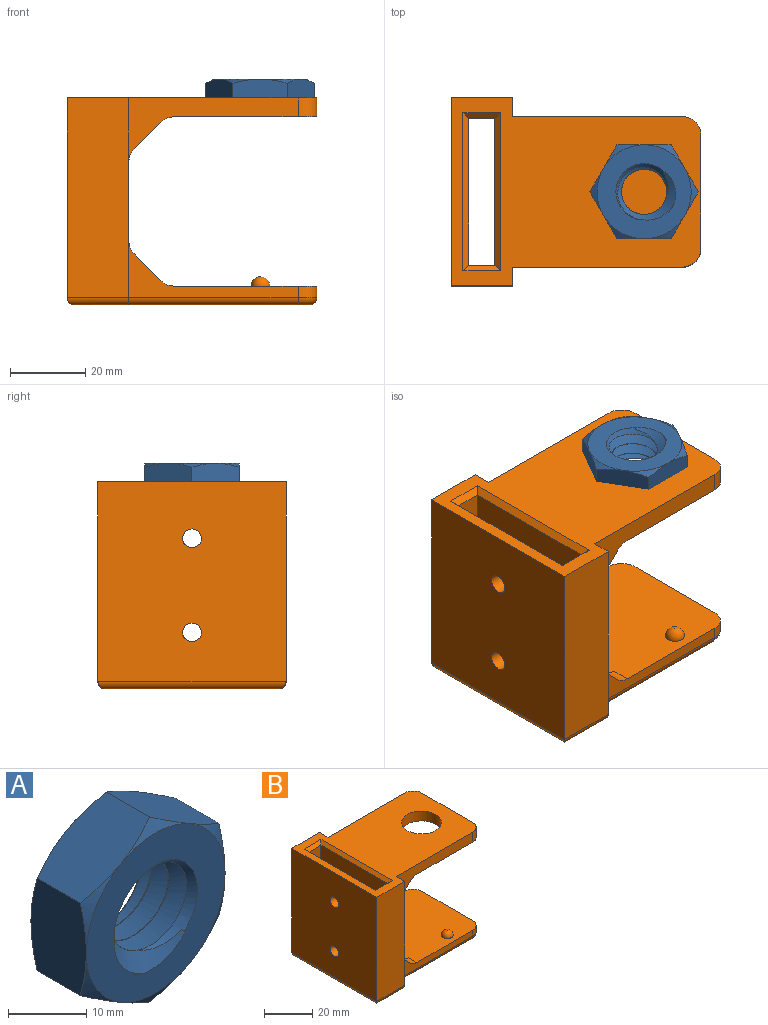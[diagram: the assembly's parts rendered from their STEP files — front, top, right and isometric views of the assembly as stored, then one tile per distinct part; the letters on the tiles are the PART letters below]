
ASSEMBLY  parts=2 mates=1
PART A: 26 faces, bbox 30.1x15x30.1 mm
  f0: cylinder r=6mm len=12mm, axis (0,1,0), area 8.6mm2, adj f21,f22,f23,f24
  f1: plane 25.37x25.37mm, normal (0,-1,0), area 303.3mm2, adj f5,f6,f8,f10,f12,f14,f22,f23
  f2: plane 25.48x25.48mm, normal (0,1,0), area 303mm2, adj f3,f4,f7,f9,f11,f13,f21,f23
  f3: cone r=20.25mm half-angle=60deg, axis (0,-1,0), area 15.4mm2, adj f2,f15,f16
  f4: cone r=20.25mm half-angle=60deg, axis (0,-1,0), area 15.4mm2, adj f2,f15,f20
  f5: cone r=20.25mm half-angle=60deg, axis (0,1,0), area 15.4mm2, adj f1,f15,f16
  f6: cone r=20.25mm half-angle=60deg, axis (0,1,0), area 15.4mm2, adj f1,f15,f20
  f7: cone r=20.25mm half-angle=60deg, axis (0,-1,0), area 15.4mm2, adj f2,f16,f17
  f8: cone r=20.25mm half-angle=60deg, axis (0,1,0), area 15.4mm2, adj f1,f16,f17
  f9: cone r=20.25mm half-angle=60deg, axis (0,-1,0), area 15.4mm2, adj f2,f17,f18
  f10: cone r=20.25mm half-angle=60deg, axis (0,1,0), area 15.4mm2, adj f1,f17,f18
  f11: cone r=20.25mm half-angle=60deg, axis (0,-1,0), area 15.4mm2, adj f2,f18,f19
  f12: cone r=20.25mm half-angle=60deg, axis (0,1,0), area 15.4mm2, adj f1,f18,f19
  f13: cone r=20.25mm half-angle=60deg, axis (0,-1,0), area 15.4mm2, adj f2,f19,f20
  f14: cone r=20.25mm half-angle=60deg, axis (0,1,0), area 15.4mm2, adj f1,f19,f20
  f15: plane 15.63x11.2mm, normal (1,0,0), area 133.3mm2, adj f3,f4,f5,f6,f16,f20
  f16: plane 13.69x11.19mm, normal (0.5,0,-0.87), area 133.3mm2, adj f3,f5,f7,f8,f15,f17
  f17: plane 13.69x11.19mm, normal (-0.5,0,-0.87), area 133.3mm2, adj f7,f8,f9,f10,f16,f18
  f18: plane 15.63x11.2mm, normal (-1,0,0), area 133.3mm2, adj f9,f10,f11,f12,f17,f19
  f19: plane 13.69x11.19mm, normal (-0.5,0,0.87), area 133.3mm2, adj f11,f12,f13,f14,f18,f20
  f20: plane 13.69x11.19mm, normal (0.5,0,0.87), area 133.3mm2, adj f4,f6,f13,f14,f15,f19
  f21: cone r=7.5mm half-angle=45deg, axis (0,1,0), area 28.9mm2, adj f0,f2,f23,f24
  f22: cone r=6mm half-angle=45deg, axis (0,-1,0), area 29.4mm2, adj f0,f1,f23,f24,f25
  f23: bspline ~19.86x17.2mm, area 410.3mm2, adj f0,f1,f2,f21,f22,f24
  f24: bspline ~19.86x17.2mm, area 410.2mm2, adj f0,f1,f2,f21,f22,f23,f25
  f25: plane 0.42x0.39mm, normal (-0.72,0,-0.69), area 0mm2, adj f1,f22,f24
PART B: 61 faces, bbox 66.8x50x55 mm
  f0: plane 7.07x7.07mm, normal (0.71,0,-0.71), area 50mm2, adj f11,f29,f39,f45
  f1: cylinder r=2.5mm len=5mm, axis (-1,0,0), area 74.6mm2, adj f8,f21
  f2: plane 7.07x7.07mm, normal (0.71,0,0.71), area 50mm2, adj f12,f28,f40,f46
  f3: cylinder r=2.5mm len=5mm, axis (-1,0,0), area 74.6mm2, adj f8,f21
  f4: plane 62.4x46mm, normal (0,0,-1), area 1965.5mm2, adj f14,f18,f31,f32,f33,f34,f53,f54
  f5: plane 66.4x50mm, normal (0,0,1), area 2174.4mm2, adj f10,f11,f12,f13,f14,f15,f16,f17
  f6: plane 30x3mm, normal (1,0,0), area 90mm2, adj f7,f48,f50,f55
  f7: plane 50x40mm, normal (0,0,1), area 1829.3mm2, adj f6,f8,f11,f12,f27,f28,f40,f43
  f8: plane 45x40mm, normal (1,0,0), area 1519.3mm2, adj f1,f3,f7,f9,f11,f12,f27,f28
  f9: plane 50x40mm, normal (0,0,-1), area 1654.7mm2, adj f8,f10,f11,f12,f13,f29,f30,f39
  f10: plane 30x5mm, normal (1,0,0), area 150mm2, adj f5,f9,f47,f49
  f11: plane 53x45.1mm, normal (0,1,0), area 467.5mm2, adj f0,f5,f7,f8,f9,f18,f24,f39
  f12: plane 53x45.1mm, normal (0,-1,0), area 467.5mm2, adj f2,f5,f7,f8,f9,f14,f23,f40
  f13: cylinder r=8.25mm len=16.5mm, axis (0,0,1), area 259.2mm2, adj f5,f9
  f14: plane 55x7mm, normal (1,0,0), area 275mm2, adj f4,f5,f12,f15,f57,f60
  f15: plane 53x16.3mm, normal (0,-1,0), area 863.9mm2, adj f5,f14,f17,f60
  f16: plane 53x16.3mm, normal (0,1,0), area 863.9mm2, adj f5,f17,f18,f58
  f17: plane 53x50mm, normal (-1,0,0), area 2610.7mm2, adj f5,f15,f16,f25,f26,f59
  f18: plane 55x7mm, normal (1,0,0), area 275mm2, adj f4,f5,f11,f16,f53,f58
  f19: plane 52x39mm, normal (1,0,0), area 1988.7mm2, adj f20,f22,f25,f26,f32,f36
  f20: plane 52x7mm, normal (0,-1,0), area 364mm2, adj f19,f21,f34,f35
  f21: plane 52x39mm, normal (-1,0,0), area 1988.7mm2, adj f1,f3,f20,f22,f33,f37
  f22: plane 52x7mm, normal (0,1,0), area 364mm2, adj f19,f21,f31,f38
  f23: plane 7.07x7.07mm, normal (0.71,0,-0.71), area 50mm2, adj f12,f30,f41,f44
  f24: plane 7.07x7.07mm, normal (0.71,0,0.71), area 50mm2, adj f11,f27,f42,f43
  f25: cylinder r=2.5mm len=5mm, axis (-1,0,0), area 73mm2, adj f17,f19
  f26: cylinder r=2.5mm len=5mm, axis (-1,0,0), area 73mm2, adj f17,f19
  f27: plane 12.07x12.07mm, normal (0,-1,0), area 51.1mm2, adj f7,f8,f24,f42,f43
  f28: plane 12.07x12.07mm, normal (0,1,0), area 51.1mm2, adj f2,f7,f8,f40,f46
  f29: plane 12.07x12.07mm, normal (0,-1,0), area 51.1mm2, adj f0,f8,f9,f39,f45
  f30: plane 12.07x12.07mm, normal (0,1,0), area 51.1mm2, adj f8,f9,f23,f41,f44
  f31: plane 10x1.5mm, normal (0,0.71,-0.71), area 18mm2, adj f4,f22,f32,f33
  f32: plane 42x1.5mm, normal (0.71,0,-0.71), area 85.9mm2, adj f4,f19,f31,f34
  f33: plane 42x1.5mm, normal (-0.71,0,-0.71), area 85.9mm2, adj f4,f21,f31,f34
  f34: plane 10x1.5mm, normal (0,-0.71,-0.71), area 18mm2, adj f4,f20,f32,f33
  f35: plane 10x1.5mm, normal (0,-0.71,0.71), area 18mm2, adj f5,f20,f36,f37
  f36: plane 42x1.5mm, normal (0.71,0,0.71), area 85.9mm2, adj f5,f19,f35,f38
  f37: plane 42x1.5mm, normal (-0.71,0,0.71), area 85.9mm2, adj f5,f21,f35,f38
  f38: plane 10x1.5mm, normal (0,0.71,0.71), area 18mm2, adj f5,f22,f36,f37
  f39: cylinder r=5mm len=5mm, axis (0,1,0), area 19.6mm2, adj f0,f9,f11,f29
  f40: cylinder r=5mm len=5mm, axis (0,-1,0), area 19.6mm2, adj f2,f7,f12,f28
  f41: cylinder r=5mm len=5mm, axis (0,-1,0), area 19.6mm2, adj f8,f12,f23,f30
  f42: cylinder r=5mm len=5mm, axis (0,1,0), area 19.6mm2, adj f8,f11,f24,f27
  f43: cylinder r=5mm len=5mm, axis (0,-1,0), area 19.6mm2, adj f7,f11,f24,f27
  f44: cylinder r=5mm len=5mm, axis (0,1,0), area 19.6mm2, adj f9,f12,f23,f30
  f45: cylinder r=5mm len=5mm, axis (0,-1,0), area 19.6mm2, adj f0,f8,f11,f29
  f46: cylinder r=5mm len=5mm, axis (0,1,0), area 19.6mm2, adj f2,f8,f12,f28
  f47: cylinder r=5mm len=5mm, axis (0,0,1), area 39.3mm2, adj f5,f9,f10,f12
  f48: cylinder r=5mm len=5mm, axis (0,0,1), area 23.6mm2, adj f6,f7,f12,f56
  f49: cylinder r=5mm len=5mm, axis (0,0,-1), area 39.3mm2, adj f5,f9,f10,f11
  f50: cylinder r=5mm len=5mm, axis (0,0,-1), area 23.6mm2, adj f6,f7,f11,f54
  f51: sphere r=2.5mm, area 39.3mm2, adj f7
  f52: sphere r=2.5mm, area 39.3mm2, adj f7
  f53: cylinder r=2mm len=45.1mm, axis (-1,0,0), area 141.7mm2, adj f4,f11,f18,f54
  f54: torus R=3mm, axis (0,0,1), area 21.1mm2, adj f4,f50,f53,f55
  f55: cylinder r=2mm len=30mm, axis (0,-1,0), area 94.2mm2, adj f4,f6,f54,f56
  f56: torus R=3mm, axis (0,0,1), area 21.1mm2, adj f4,f48,f55,f57
  f57: cylinder r=2mm len=45.1mm, axis (1,0,0), area 141.7mm2, adj f4,f12,f14,f56
  f58: cylinder r=2mm len=16.3mm, axis (1,0,0), area 48.9mm2, adj f4,f16,f18,f59
  f59: cylinder r=2mm len=50mm, axis (0,-1,0), area 152.5mm2, adj f4,f17,f58,f60
  f60: cylinder r=2mm len=16.3mm, axis (-1,0,0), area 48.9mm2, adj f4,f14,f15,f59
PLACE A rot(axis=(-0.58,-0.58,0.58),120deg) t=(51.65,45.19,65.88)mm
PLACE B t=(16.65,25.19,15.88)mm
MATE fastened A.f0 <-> B.f13  axis (0,0,-1) through (51.65,45.19,65.88)mm
